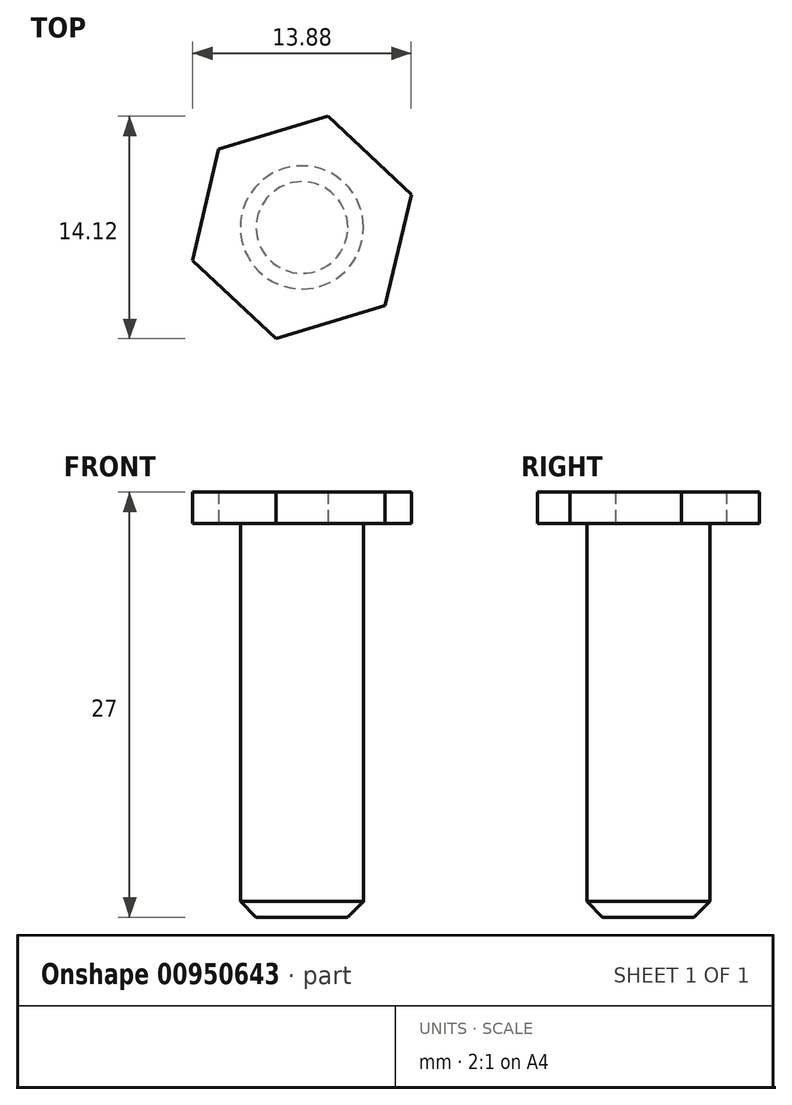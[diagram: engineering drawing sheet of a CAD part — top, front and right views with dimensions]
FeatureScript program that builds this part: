
annotation { "Feature Type Name" : "Feature", "Feature Type Description" : "" }
export const myFeature = defineFeature(function(context is Context, id is Id, definition is map)
    precondition{}
    {
        {
            var Q0;
            Q0=qCreatedBy(makeId("Top.planeOp"),FACE);
            var sketch = newSketch(context, id + "F0", { "sketchPlane" : qUnion([Q0])});
            skCircle(sketch, "E0", {"center": v(0, 0) * mm, "radius": 3.91 * mm});
            skCircle(sketch, "E1.cCircle", {"center": v(0, 0) * mm, "radius": 7.25 * mm, "construction": true});
            skLineSegment(sketch, "E1.0", {"start": v(6.94, 2.1) * mm, "end": v(5.28, -4.96) * mm});
            skLineSegment(sketch, "E1.1", {"start": v(5.28, -4.96) * mm, "end": v(-1.66, -7.06) * mm});
            skLineSegment(sketch, "E1.2", {"start": v(-1.66, -7.06) * mm, "end": v(-6.94, -2.1) * mm});
            skLineSegment(sketch, "E1.3", {"start": v(-6.94, -2.1) * mm, "end": v(-5.28, 4.96) * mm});
            skLineSegment(sketch, "E1.4", {"start": v(-5.28, 4.96) * mm, "end": v(1.66, 7.06) * mm});
            skLineSegment(sketch, "E1.5", {"start": v(1.66, 7.06) * mm, "end": v(6.94, 2.1) * mm});
            skSolve(sketch);
        }
        {
            var Q0;
            Q0=makeQuery(id+"F0.imprint","IMPRINT",FACE,{"disambiguationData":[TD([[makeQuery(id+"F0.imprint","IMPRINT",EDGE,{"derivedFrom":sQuery(id+"F0.wireOp",EDGE,"E0")}),1.0]])]});
            extrude(context, id + "F1", {"entities" : qUnion([Q0]), "oppositeDirection" : true, "depth" : 25 * mm, "offsetDistance" : 25 * mm});
        }
        {
            var Q0;
            Q0 = qSketchRegion(id + "F0", true);
            var Q1;
            Q1=makeQuery(id+"F1.opExtrude","CAP_FACE",FACE,{"disambiguationData":[OSD([sQuery(id+"F0.wireOp",EDGE,"E0")])],"isStart":true});
            extrude(context, id + "F2", {"entities" : qUnion([Q0, Q1]), "operationType" : NewBodyOperationType.ADD, "depth" : 2 * mm, "offsetDistance" : 25 * mm});
        }
        {
            var Q0;
            Q0=makeQuery(id+"F1.opExtrude","CAP_EDGE",EDGE,{"disambiguationData":[OSD([sQuery(id+"F0.wireOp",EDGE,"E0")])],"isStart":false});
            chamfer(context, id + "F3", {"entities" : qUnion([Q0]), "width" : 1 * mm, "tangentPropagation" : true});
        }
    });
